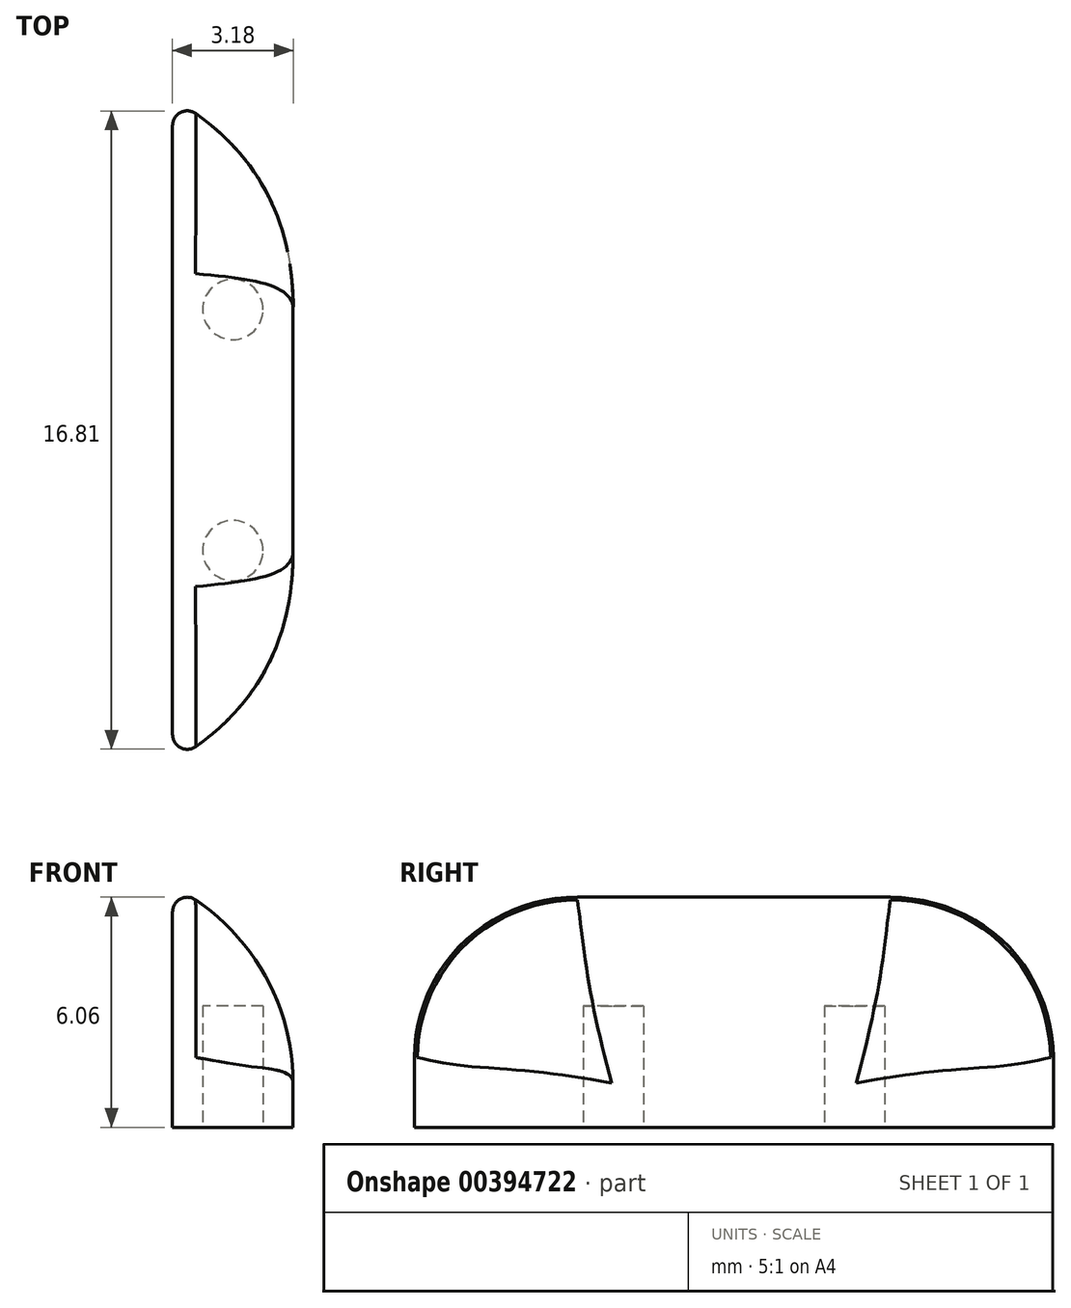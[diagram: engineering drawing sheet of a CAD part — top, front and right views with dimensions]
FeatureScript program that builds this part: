
annotation { "Feature Type Name" : "Feature", "Feature Type Description" : "" }
export const myFeature = defineFeature(function(context is Context, id is Id, definition is map)
    precondition{}
    {
        {
            var Q0;
            Q0=qCreatedBy(makeId("Top.planeOp"),FACE);
            var sketch = newSketch(context, id + "F0", { "sketchPlane" : qUnion([Q0])});
            skCircle(sketch, "E0", {"center": v(0, -6.35) * mm, "radius": 0.8 * mm});
            skCircle(sketch, "E1", {"center": v(0, 0) * mm, "radius": 0.8 * mm});
            skLineSegment(sketch, "E2", {"start": v(0, 0) * mm, "end": v(0, -6.35) * mm});
            skLineSegment(sketch, "E3.bottom", {"start": v(-1.59, 5.56) * mm, "end": v(1.59, 5.56) * mm});
            skLineSegment(sketch, "E3.top", {"start": v(-1.59, -11.9) * mm, "end": v(1.59, -11.9) * mm});
            skLineSegment(sketch, "E3.left", {"start": v(-1.59, 5.56) * mm, "end": v(-1.59, -11.9) * mm});
            skLineSegment(sketch, "E3.right", {"start": v(1.59, 5.56) * mm, "end": v(1.59, -11.9) * mm});
            skLineSegment(sketch, "E4", {"start": v(0, 0) * mm, "end": v(0, 5.56) * mm});
            skLineSegment(sketch, "E5", {"start": v(0, -6.35) * mm, "end": v(0, -11.9) * mm});
            skLineSegment(sketch, "E6", {"start": v(0, -3.17) * mm, "end": v(-1.59, -3.17) * mm});
            skLineSegment(sketch, "E7", {"start": v(0, -3.17) * mm, "end": v(1.59, -3.17) * mm});
            skSolve(sketch);
        }
        {
            var Q0;
            Q0=makeQuery(id+"F0.imprint","IMPRINT",FACE,{"disambiguationData":[TD([[makeQuery(id+"F0.imprint","IMPRINT",EDGE,{"derivedFrom":sQuery(id+"F0.wireOp",EDGE,"E0")}),-1.0]])]});
            var Q1;
            {var subQ0=sQuery(id+"F0.wireOp",EDGE,"E2");var subQ1=sQuery(id+"F0.wireOp",EDGE,"E0");var subQ2=makeQuery(id+"F0.imprint","INTERSECT",VERTEX,{"derivedFrom":[subQ1,subQ0]});Q1=makeQuery(id+"F0.imprint","IMPRINT",FACE,{"disambiguationData":[TD([[makeQuery(id+"F0.imprint","IMPRINT",EDGE,{"disambiguationData":[TD([[subQ2,-1.0]])],"derivedFrom":subQ1}),1.0]])]});}
            var Q2;
            {var subQ3=sQuery(id+"F0.wireOp",EDGE,"E7");Q2=makeQuery(id+"F0.imprint","IMPRINT",FACE,{"disambiguationData":[TD([[makeQuery(id+"F0.imprint","IMPRINT",EDGE,{"derivedFrom":subQ3}),1.0]])]});}
            var Q3;
            {var subQ0=sQuery(id+"F0.wireOp",EDGE,"E2");var subQ1=sQuery(id+"F0.wireOp",EDGE,"E1");var subQ2=makeQuery(id+"F0.imprint","INTERSECT",VERTEX,{"derivedFrom":[subQ1,subQ0]});Q3=makeQuery(id+"F0.imprint","IMPRINT",FACE,{"disambiguationData":[TD([[makeQuery(id+"F0.imprint","IMPRINT",EDGE,{"disambiguationData":[TD([[subQ2,1.0]])],"derivedFrom":subQ1}),1.0]])]});}
            var Q4;
            {var subQ5=sQuery(id+"F0.wireOp",EDGE,"E6");Q4=makeQuery(id+"F0.imprint","IMPRINT",FACE,{"disambiguationData":[TD([[makeQuery(id+"F0.imprint","IMPRINT",EDGE,{"derivedFrom":subQ5}),-1.0]])]});}
            var Q5;
            {var subQ0=sQuery(id+"F0.wireOp",EDGE,"E2");var subQ1=sQuery(id+"F0.wireOp",EDGE,"E1");var subQ2=makeQuery(id+"F0.imprint","INTERSECT",VERTEX,{"derivedFrom":[subQ1,subQ0]});Q5=makeQuery(id+"F0.imprint","IMPRINT",FACE,{"disambiguationData":[TD([[makeQuery(id+"F0.imprint","IMPRINT",EDGE,{"disambiguationData":[TD([[subQ2,-1.0]])],"derivedFrom":subQ1}),1.0]])]});}
            var Q6;
            {var subQ0=sQuery(id+"F0.wireOp",EDGE,"E2");var subQ1=sQuery(id+"F0.wireOp",EDGE,"E0");var subQ2=makeQuery(id+"F0.imprint","INTERSECT",VERTEX,{"derivedFrom":[subQ1,subQ0]});Q6=makeQuery(id+"F0.imprint","IMPRINT",FACE,{"disambiguationData":[TD([[makeQuery(id+"F0.imprint","IMPRINT",EDGE,{"disambiguationData":[TD([[subQ2,1.0]])],"derivedFrom":subQ1}),1.0]])]});}
            extrude(context, id + "F1", {"entities" : qUnion([Q0, Q1, Q2, Q3, Q4, Q5, Q6]), "depth" : 6.35 * mm});
        }
        {
            var Q0;
            Q0=makeQuery(id+"F1.opExtrude","CAP_EDGE",EDGE,{"disambiguationData":[OSD([sQuery(id+"F0.wireOp",EDGE,"E3.right")])],"isStart":false});
            fillet(context, id + "F2", {"entities" : qUnion([Q0]), "radius" : 5.83 * mm, "tangentPropagation" : true, "allowEdgeOverflow" : false});
        }
        {
            var Q0;
            Q0=makeQuery(id+"F2.opFillet","BLEND_EDGE",EDGE,{"blendedFrom":[makeQuery(id+"F1.opExtrude","CAP_EDGE",EDGE,{"disambiguationData":[OSD([sQuery(id+"F0.wireOp",EDGE,"E3.right")])],"isStart":false}),makeQuery(id+"F1.opExtrude","SWEPT_FACE",FACE,{"disambiguationData":[OSD([sQuery(id+"F0.wireOp",EDGE,"E3.top")])]})],"blendedInto":[makeQuery(id+"F1.opExtrude","SWEPT_FACE",FACE,{"disambiguationData":[OSD([sQuery(id+"F0.wireOp",EDGE,"E3.top")])]})]});
            var Q1;
            Q1=makeQuery(id+"F2.opFillet","BLEND_EDGE",EDGE,{"blendedFrom":[makeQuery(id+"F1.opExtrude","CAP_EDGE",EDGE,{"disambiguationData":[OSD([sQuery(id+"F0.wireOp",EDGE,"E3.right")])],"isStart":false}),makeQuery(id+"F1.opExtrude","SWEPT_FACE",FACE,{"disambiguationData":[OSD([sQuery(id+"F0.wireOp",EDGE,"E3.bottom")])]})],"blendedInto":[makeQuery(id+"F1.opExtrude","SWEPT_FACE",FACE,{"disambiguationData":[OSD([sQuery(id+"F0.wireOp",EDGE,"E3.bottom")])]})]});
            fillet(context, id + "F3", {"entities" : qUnion([Q0, Q1]), "radius" : 6.38 * mm, "tangentPropagation" : true, "rho" : 0.5, "crossSection" : FilletCrossSection.CONIC, "allowEdgeOverflow" : false});
        }
        {
            var Q0;
            {var subQ0=sQuery(id+"F0.wireOp",EDGE,"E3.right");Q0=makeQuery(id+"F3.opFillet","BLEND_EDGE",EDGE,{"blendedFrom":[makeQuery(id+"F1.opExtrude","SWEPT_EDGE",EDGE,{"disambiguationData":[OSD([sQuery(id+"F0.wireOp",EDGE,"E3.top"),subQ0])]}),makeQuery(id+"F2.opFillet","BLEND_FACE",FACE,{"disambiguationData":[OSD([subQ0])]})],"blendedInto":[makeQuery(id+"F2.opFillet","BLEND_FACE",FACE,{"disambiguationData":[OSD([subQ0])]})]});}
            var Q1;
            {var subQ0=sQuery(id+"F0.wireOp",EDGE,"E3.right");Q1=makeQuery(id+"F3.opFillet","BLEND_EDGE",EDGE,{"blendedFrom":[makeQuery(id+"F1.opExtrude","SWEPT_EDGE",EDGE,{"disambiguationData":[OSD([sQuery(id+"F0.wireOp",EDGE,"E3.bottom"),subQ0])]}),makeQuery(id+"F2.opFillet","BLEND_FACE",FACE,{"disambiguationData":[OSD([subQ0])]})],"blendedInto":[makeQuery(id+"F2.opFillet","BLEND_FACE",FACE,{"disambiguationData":[OSD([subQ0])]})]});}
            fillet(context, id + "F4", {"entities" : qUnion([Q0, Q1]), "radius" : 5.08 * mm, "tangentPropagation" : true, "allowEdgeOverflow" : false});
        }
        {
            var Q0;
            Q0=makeQuery(id+"F2.opFillet","BLEND_EDGE",EDGE,{"blendedFrom":[makeQuery(id+"F1.opExtrude","CAP_EDGE",EDGE,{"disambiguationData":[OSD([sQuery(id+"F0.wireOp",EDGE,"E3.right")])],"isStart":false}),makeQuery(id+"F1.opExtrude","SWEPT_FACE",FACE,{"disambiguationData":[OSD([sQuery(id+"F0.wireOp",EDGE,"E3.left")])]})],"blendedInto":[makeQuery(id+"F1.opExtrude","SWEPT_FACE",FACE,{"disambiguationData":[OSD([sQuery(id+"F0.wireOp",EDGE,"E3.left")])]})]});
            fillet(context, id + "F5", {"entities" : qUnion([Q0]), "radius" : 0.39 * mm, "tangentPropagation" : true, "allowEdgeOverflow" : false});
        }
        {
            var Q0;
            {var subQ0=sQuery(id+"F0.wireOp",EDGE,"E2");var subQ1=sQuery(id+"F0.wireOp",EDGE,"E0");var subQ2=makeQuery(id+"F0.imprint","INTERSECT",VERTEX,{"derivedFrom":[subQ1,subQ0]});Q0=makeQuery(id+"F0.imprint","IMPRINT",FACE,{"disambiguationData":[TD([[makeQuery(id+"F0.imprint","IMPRINT",EDGE,{"disambiguationData":[TD([[subQ2,1.0]])],"derivedFrom":subQ1}),1.0]])]});}
            var Q1;
            {var subQ0=sQuery(id+"F0.wireOp",EDGE,"E2");var subQ1=sQuery(id+"F0.wireOp",EDGE,"E0");var subQ2=makeQuery(id+"F0.imprint","INTERSECT",VERTEX,{"derivedFrom":[subQ1,subQ0]});Q1=makeQuery(id+"F0.imprint","IMPRINT",FACE,{"disambiguationData":[TD([[makeQuery(id+"F0.imprint","IMPRINT",EDGE,{"disambiguationData":[TD([[subQ2,-1.0]])],"derivedFrom":subQ1}),1.0]])]});}
            var Q2;
            {var subQ0=sQuery(id+"F0.wireOp",EDGE,"E2");var subQ1=sQuery(id+"F0.wireOp",EDGE,"E1");var subQ2=makeQuery(id+"F0.imprint","INTERSECT",VERTEX,{"derivedFrom":[subQ1,subQ0]});Q2=makeQuery(id+"F0.imprint","IMPRINT",FACE,{"disambiguationData":[TD([[makeQuery(id+"F0.imprint","IMPRINT",EDGE,{"disambiguationData":[TD([[subQ2,1.0]])],"derivedFrom":subQ1}),1.0]])]});}
            var Q3;
            {var subQ0=sQuery(id+"F0.wireOp",EDGE,"E2");var subQ1=sQuery(id+"F0.wireOp",EDGE,"E1");var subQ2=makeQuery(id+"F0.imprint","INTERSECT",VERTEX,{"derivedFrom":[subQ1,subQ0]});Q3=makeQuery(id+"F0.imprint","IMPRINT",FACE,{"disambiguationData":[TD([[makeQuery(id+"F0.imprint","IMPRINT",EDGE,{"disambiguationData":[TD([[subQ2,-1.0]])],"derivedFrom":subQ1}),1.0]])]});}
            extrude(context, id + "F6", {"entities" : qUnion([Q0, Q1, Q2, Q3]), "operationType" : NewBodyOperationType.REMOVE, "depth" : 3.2 * mm});
        }
    });
